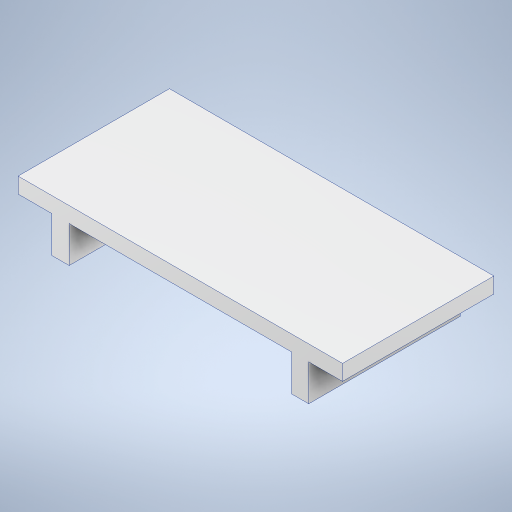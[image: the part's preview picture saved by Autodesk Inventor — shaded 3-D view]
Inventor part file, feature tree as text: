
AUTODESK INVENTOR PART (.ipt)
format: ipt  version: 2024 (Build 280153000, 153)  size: 248,320 bytes
history: native  units: mm
features: extrude x3, sketch x3, projected_geometry x1
ambient origin geometry x8: Origin, YZ Plane, XZ Plane, XY Plane, X Axis, Y Axis, Z Axis, Center Point
bodies: Solid1 (feature_tree)
feature tree (7):
  extrude  "Extrusion1"  Depth=175.0mm
  extrude  "Extrusion2"  Depth=18.0mm TaperAngle=0.0deg
  extrude  "Extrusion3"  Depth=39.0535mm
  sketch  "Sketch1"  dims[d0=175.0mm d1=175.0mm]
  sketch  "Sketch2"  dims[d2=12.0mm d3=0.0mm d6=18.0mm d7=0.0mm]
  sketch  "Sketch3"  dims[d8=100.0mm d9=100.0mm d10=256.893mm d11=20.0mm d12=20.0mm d13=39.0535mm d14=39.0535mm d15=48.0mm d16=0.0mm]
  projected_geometry  "Projected Loop1"
